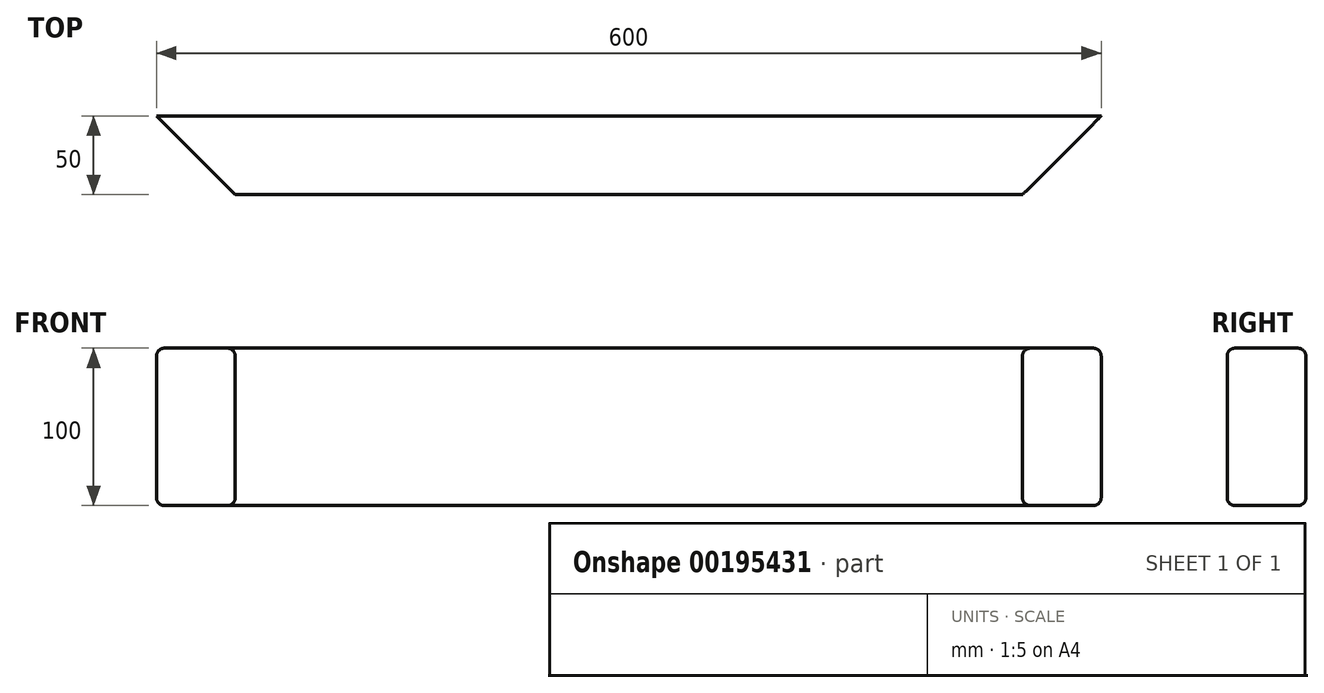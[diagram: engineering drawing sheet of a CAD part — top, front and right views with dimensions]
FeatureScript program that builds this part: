
annotation { "Feature Type Name" : "Feature", "Feature Type Description" : "" }
export const myFeature = defineFeature(function(context is Context, id is Id, definition is map)
    precondition{}
    {
        {
            var Q0;
            Q0=qCreatedBy(makeId("Front.planeOp"),FACE);
            var sketch = newSketch(context, id + "F0", { "sketchPlane" : qUnion([Q0])});
            skLineSegment(sketch, "E0.bottom", {"start": v(-50.34, 0) * mm, "end": v(-650.34, 0) * mm});
            skLineSegment(sketch, "E0.top", {"start": v(-50.34, 100) * mm, "end": v(-650.34, 100) * mm});
            skLineSegment(sketch, "E0.left", {"start": v(-50.34, 0) * mm, "end": v(-50.34, 100) * mm});
            skLineSegment(sketch, "E0.right", {"start": v(-650.34, 0) * mm, "end": v(-650.34, 100) * mm});
            skSolve(sketch);
        }
        {
            var Q0;
            Q0=qSketchRegion(id+"F0",true);
            extrude(context, id + "F3", {"entities" : qUnion([Q0]), "depth" : 50 * mm});
        }
        {
            var Q0;
            Q0=makeQuery(id+"F3.opExtrude","CAP_EDGE",EDGE,{"disambiguationData":[OSD([sQuery(id+"F0.wireOp",EDGE,"E0.left")])],"isStart":false});
            chamfer(context, id + "F1", {"entities" : qUnion([Q0]), "width" : 50 * mm, "tangentPropagation" : true});
        }
        {
            var Q0;
            Q0=makeQuery(id+"F3.opExtrude","CAP_EDGE",EDGE,{"disambiguationData":[OSD([sQuery(id+"F0.wireOp",EDGE,"E0.right")])],"isStart":false});
            chamfer(context, id + "F4", {"entities" : qUnion([Q0]), "width" : 50 * mm, "tangentPropagation" : true});
        }
        {
            var Q0;
            Q0=makeQuery(id+"F3.opExtrude","CAP_EDGE",EDGE,{"disambiguationData":[OSD([sQuery(id+"F0.wireOp",EDGE,"E0.bottom")])],"isStart":false});
            var Q1;
            Q1=makeQuery(id+"F3.opExtrude","CAP_EDGE",EDGE,{"disambiguationData":[OSD([sQuery(id+"F0.wireOp",EDGE,"E0.top")])],"isStart":false});
            var Q2;
            Q2=makeQuery(id+"F3.opExtrude","CAP_EDGE",EDGE,{"disambiguationData":[OSD([sQuery(id+"F0.wireOp",EDGE,"E0.top")])],"isStart":true});
            var Q3;
            Q3=makeQuery(id+"F3.opExtrude","CAP_EDGE",EDGE,{"disambiguationData":[OSD([sQuery(id+"F0.wireOp",EDGE,"E0.bottom")])],"isStart":true});
            fillet(context, id + "F2", {"entities" : qUnion([Q0, Q1, Q2, Q3]), "radius" : 5 * mm, "tangentPropagation" : true, "allowEdgeOverflow" : false});
        }
    });
